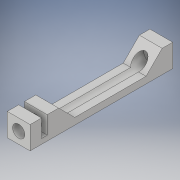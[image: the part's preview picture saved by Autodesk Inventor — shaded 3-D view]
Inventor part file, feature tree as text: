
AUTODESK INVENTOR PART (.ipt)
format: ipt  version: 2019.4 (Build 234330000, 330)  size: 288,256 bytes
history: native  units: in
note: dims shown in document units (in); Inventor stores cm internally (conversion verified against a paired STEP export)
features: extrude x5, sketch x5
ambient origin geometry x8: Origin, YZ Plane, XZ Plane, XY Plane, X Axis, Y Axis, Z Axis, Center Point
bodies: Solid1 (feature_tree)
feature tree (10):
  extrude  "Extrusion1"  Depth=1.9685in
  extrude  "Extrusion2"  Depth=0.315in
  extrude  "Extrusion3"  Depth=0.0787in
  extrude  "Extrusion4"  Depth=0.2441in TaperAngle=0.0deg
  extrude  "Extrusion5"  Depth=0.1575in
  sketch  "Sketch1"  dims[d0=0.315in d1=1.9685in]
  sketch  "Sketch2"  dims[d2=0.315in d3=0.0in d4=0.1693in]
  sketch  "Sketch3"  dims[d5=0.1575in d6=0.0in d8=0.0787in]
  sketch  "Sketch4"  dims[d9=0.1575in d10=0.2441in d11=0.0in]
  sketch  "Sketch5"  dims[d12=1.5748in d13=0.0in d14=0.1575in d15=0.315in d16=135.0deg d17=0.9843in d18=135.0deg d19=1.5748in d20=0.0in]
